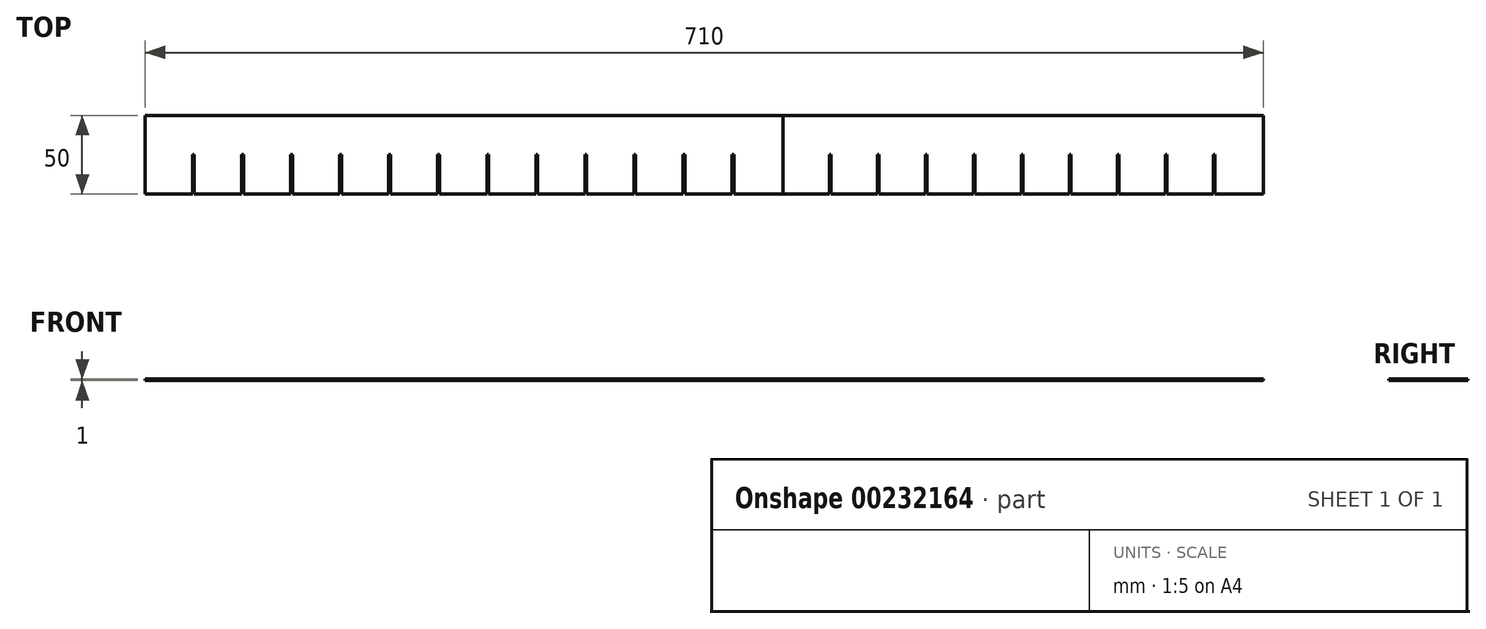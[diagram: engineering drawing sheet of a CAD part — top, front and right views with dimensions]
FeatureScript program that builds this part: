
annotation { "Feature Type Name" : "Feature", "Feature Type Description" : "" }
export const myFeature = defineFeature(function(context is Context, id is Id, definition is map)
    precondition{}
    {
        {
            var Q0;
            Q0=qCreatedBy(makeId("Top.planeOp"),FACE);
            var sketch = newSketch(context, id + "F0", { "sketchPlane" : qUnion([Q0])});
            skLineSegment(sketch, "E0.bottom", {"start": v(0, 50) * mm, "end": v(405, 50) * mm});
            skLineSegment(sketch, "E0.top", {"start": v(0, 0) * mm, "end": v(405, 0) * mm});
            skLineSegment(sketch, "E0.left", {"start": v(0, 50) * mm, "end": v(0, 0) * mm});
            skLineSegment(sketch, "E0.right", {"start": v(405, 50) * mm, "end": v(405, 0) * mm});
            skLineSegment(sketch, "E1", {"start": v(30.05, 0) * mm, "end": v(30.05, 25) * mm});
            skPoint(sketch, "E1.endSnap0", {"position": v(0, 25) * mm});
            skLineSegment(sketch, "E2", {"start": v(31.15, 25) * mm, "end": v(31.15, 0) * mm});
            skLineSegment(sketch, "E3", {"start": v(31.15, 25) * mm, "end": v(30.05, 25) * mm});
            skLineSegment(sketch, "E4.1.0.0", {"start": v(62.3, 25) * mm, "end": v(62.3, 0) * mm});
            skLineSegment(sketch, "E4.1.0.1", {"start": v(61.2, 0) * mm, "end": v(61.2, 25) * mm});
            skLineSegment(sketch, "E4.1.0.2", {"start": v(62.3, 25) * mm, "end": v(61.2, 25) * mm});
            skLineSegment(sketch, "E4.2.0.0", {"start": v(93.45, 25) * mm, "end": v(93.45, 0) * mm});
            skLineSegment(sketch, "E4.2.0.1", {"start": v(92.35, 0) * mm, "end": v(92.35, 25) * mm});
            skLineSegment(sketch, "E4.2.0.2", {"start": v(93.45, 25) * mm, "end": v(92.35, 25) * mm});
            skLineSegment(sketch, "E4.3.0.0", {"start": v(124.6, 25) * mm, "end": v(124.6, 0) * mm});
            skLineSegment(sketch, "E4.3.0.1", {"start": v(123.5, 0) * mm, "end": v(123.5, 25) * mm});
            skLineSegment(sketch, "E4.3.0.2", {"start": v(124.6, 25) * mm, "end": v(123.5, 25) * mm});
            skLineSegment(sketch, "E4.4.0.0", {"start": v(155.75, 25) * mm, "end": v(155.75, 0) * mm});
            skLineSegment(sketch, "E4.4.0.1", {"start": v(154.65, 0) * mm, "end": v(154.65, 25) * mm});
            skLineSegment(sketch, "E4.4.0.2", {"start": v(155.75, 25) * mm, "end": v(154.65, 25) * mm});
            skLineSegment(sketch, "E4.5.0.0", {"start": v(186.9, 25) * mm, "end": v(186.9, 0) * mm});
            skLineSegment(sketch, "E4.5.0.1", {"start": v(185.8, 0) * mm, "end": v(185.8, 25) * mm});
            skLineSegment(sketch, "E4.5.0.2", {"start": v(186.9, 25) * mm, "end": v(185.8, 25) * mm});
            skLineSegment(sketch, "E4.6.0.0", {"start": v(218.05, 25) * mm, "end": v(218.05, 0) * mm});
            skLineSegment(sketch, "E4.6.0.1", {"start": v(216.95, 0) * mm, "end": v(216.95, 25) * mm});
            skLineSegment(sketch, "E4.6.0.2", {"start": v(218.05, 25) * mm, "end": v(216.95, 25) * mm});
            skLineSegment(sketch, "E4.7.0.0", {"start": v(249.2, 25) * mm, "end": v(249.2, 0) * mm});
            skLineSegment(sketch, "E4.7.0.1", {"start": v(248.1, 0) * mm, "end": v(248.1, 25) * mm});
            skLineSegment(sketch, "E4.7.0.2", {"start": v(249.2, 25) * mm, "end": v(248.1, 25) * mm});
            skLineSegment(sketch, "E4.8.0.0", {"start": v(280.35, 25) * mm, "end": v(280.35, 0) * mm});
            skLineSegment(sketch, "E4.8.0.1", {"start": v(279.25, 0) * mm, "end": v(279.25, 25) * mm});
            skLineSegment(sketch, "E4.8.0.2", {"start": v(280.35, 25) * mm, "end": v(279.25, 25) * mm});
            skLineSegment(sketch, "E4.9.0.0", {"start": v(311.5, 25) * mm, "end": v(311.5, 0) * mm});
            skLineSegment(sketch, "E4.9.0.1", {"start": v(310.4, 0) * mm, "end": v(310.4, 25) * mm});
            skLineSegment(sketch, "E4.9.0.2", {"start": v(311.5, 25) * mm, "end": v(310.4, 25) * mm});
            skLineSegment(sketch, "E4.10.0.0", {"start": v(342.65, 25) * mm, "end": v(342.65, 0) * mm});
            skLineSegment(sketch, "E4.10.0.1", {"start": v(341.55, 0) * mm, "end": v(341.55, 25) * mm});
            skLineSegment(sketch, "E4.10.0.2", {"start": v(342.65, 25) * mm, "end": v(341.55, 25) * mm});
            skLineSegment(sketch, "E4.11.0.0", {"start": v(373.8, 25) * mm, "end": v(373.8, 0) * mm});
            skLineSegment(sketch, "E4.11.0.1", {"start": v(372.7, 0) * mm, "end": v(372.7, 25) * mm});
            skLineSegment(sketch, "E4.11.0.2", {"start": v(373.8, 25) * mm, "end": v(372.7, 25) * mm});
            skLineSegment(sketch, "E4.direction1", {"start": v(31.15, 0) * mm, "end": v(62.3, 0) * mm, "construction": true});
            skLineSegment(sketch, "E5.bottom", {"start": v(405, 50) * mm, "end": v(710, 50) * mm});
            skLineSegment(sketch, "E5.top", {"start": v(405, 0) * mm, "end": v(710, 0) * mm});
            skLineSegment(sketch, "E5.right", {"start": v(710, 50) * mm, "end": v(710, 0) * mm});
            skLineSegment(sketch, "E6", {"start": v(434.4, 0) * mm, "end": v(434.4, 25) * mm});
            skLineSegment(sketch, "E7", {"start": v(434.4, 25) * mm, "end": v(435.5, 25) * mm});
            skLineSegment(sketch, "E8", {"start": v(435.5, 25) * mm, "end": v(435.5, 0) * mm});
            skLineSegment(sketch, "E9.1.0.0", {"start": v(466, 25) * mm, "end": v(466, 0) * mm});
            skLineSegment(sketch, "E9.1.0.1", {"start": v(464.9, 25) * mm, "end": v(466, 25) * mm});
            skLineSegment(sketch, "E9.1.0.2", {"start": v(464.9, 0) * mm, "end": v(464.9, 25) * mm});
            skLineSegment(sketch, "E9.2.0.0", {"start": v(496.5, 25) * mm, "end": v(496.5, 0) * mm});
            skLineSegment(sketch, "E9.2.0.1", {"start": v(495.4, 25) * mm, "end": v(496.5, 25) * mm});
            skLineSegment(sketch, "E9.2.0.2", {"start": v(495.4, 0) * mm, "end": v(495.4, 25) * mm});
            skLineSegment(sketch, "E9.3.0.0", {"start": v(527, 25) * mm, "end": v(527, 0) * mm});
            skLineSegment(sketch, "E9.3.0.1", {"start": v(525.9, 25) * mm, "end": v(527, 25) * mm});
            skLineSegment(sketch, "E9.3.0.2", {"start": v(525.9, 0) * mm, "end": v(525.9, 25) * mm});
            skLineSegment(sketch, "E9.4.0.0", {"start": v(557.5, 25) * mm, "end": v(557.5, 0) * mm});
            skLineSegment(sketch, "E9.4.0.1", {"start": v(556.4, 25) * mm, "end": v(557.5, 25) * mm});
            skLineSegment(sketch, "E9.4.0.2", {"start": v(556.4, 0) * mm, "end": v(556.4, 25) * mm});
            skLineSegment(sketch, "E9.5.0.0", {"start": v(588, 25) * mm, "end": v(588, 0) * mm});
            skLineSegment(sketch, "E9.5.0.1", {"start": v(586.9, 25) * mm, "end": v(588, 25) * mm});
            skLineSegment(sketch, "E9.5.0.2", {"start": v(586.9, 0) * mm, "end": v(586.9, 25) * mm});
            skLineSegment(sketch, "E9.6.0.0", {"start": v(618.5, 25) * mm, "end": v(618.5, 0) * mm});
            skLineSegment(sketch, "E9.6.0.1", {"start": v(617.4, 25) * mm, "end": v(618.5, 25) * mm});
            skLineSegment(sketch, "E9.6.0.2", {"start": v(617.4, 0) * mm, "end": v(617.4, 25) * mm});
            skLineSegment(sketch, "E9.7.0.0", {"start": v(649, 25) * mm, "end": v(649, 0) * mm});
            skLineSegment(sketch, "E9.7.0.1", {"start": v(647.9, 25) * mm, "end": v(649, 25) * mm});
            skLineSegment(sketch, "E9.7.0.2", {"start": v(647.9, 0) * mm, "end": v(647.9, 25) * mm});
            skLineSegment(sketch, "E9.8.0.0", {"start": v(679.5, 25) * mm, "end": v(679.5, 0) * mm});
            skLineSegment(sketch, "E9.8.0.1", {"start": v(678.4, 25) * mm, "end": v(679.5, 25) * mm});
            skLineSegment(sketch, "E9.8.0.2", {"start": v(678.4, 0) * mm, "end": v(678.4, 25) * mm});
            skLineSegment(sketch, "E9.direction1", {"start": v(435.5, 0) * mm, "end": v(466, 0) * mm, "construction": true});
            skSolve(sketch);
        }
        {
            var Q0;
            Q0=makeQuery(id+"F0.imprint","IMPRINT",FACE,{"disambiguationData":[TD([[makeQuery(id+"F0.imprint","IMPRINT",EDGE,{"derivedFrom":sQuery(id+"F0.wireOp",EDGE,"E0.bottom")}),-1.0]])]});
            extrude(context, id + "F1", {"entities" : qUnion([Q0]), "depth" : 1 * mm});
        }
        {
            var Q0;
            Q0=makeQuery(id+"F0.imprint","IMPRINT",FACE,{"disambiguationData":[TD([[makeQuery(id+"F0.imprint","IMPRINT",EDGE,{"derivedFrom":sQuery(id+"F0.wireOp",EDGE,"E5.bottom")}),-1.0]])]});
            extrude(context, id + "F2", {"entities" : qUnion([Q0]), "depth" : 1 * mm});
        }
    });
